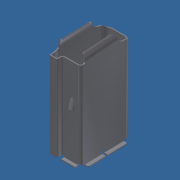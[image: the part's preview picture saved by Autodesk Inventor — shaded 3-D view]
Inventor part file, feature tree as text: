
AUTODESK INVENTOR PART (.ipt)
format: ipt  version: unknown  size: 579,072 bytes
history: native  units: mm
features: sketch x17, extrude x14, other x12, fillet x6, projected_geometry x2, shell x1
ambient origin geometry x8: Origin, YZ Plane, XZ Plane, XY Plane, X Axis, Y Axis, Z Axis, Center Point
feature tree (52):
  extrude  "Выдавливание1"  Depth=38.0mm
  other  "РабПлоскость1"
  other  "РабПлоскость2"
  sketch  "Эскиз4"
  other  "РабПлоскость3"
  extrude  "Выдавливание2"  Depth=42.0mm
  fillet  "Сопряжение7"  Radius=6.0mm
  shell  "Оболочка1"  Thickness=18.5mm
  extrude  "Выдавливание4"  Depth=10.0mm
  extrude  "Выдавливание5"  Depth=13.0mm
  fillet  "Сопряжение8"  Radius=5.0mm
  fillet  "Сопряжение9"  Radius=2.0mm
  extrude  "Выдавливание6"  Depth=64.0mm TaperAngle=0.0deg
  fillet  "Сопряжение10"  Radius=1.0mm
  fillet  "Сопряжение11"  Radius=29.0mm
  fillet  "Сопряжение12"  [1 undecoded]
  extrude  "Выдавливание7"  Depth=4.0mm
  extrude  "Выдавливание8"  Depth=6.0mm
  extrude  "Выдавливание9"  Depth=10.0mm TaperAngle=0.0deg
  other  "РабПлоскость4"
  extrude  "Выдавливание10"  Depth=0.6mm
  extrude  "Выдавливание11"  Depth=0.8mm
  other  "Сгиб детали1"
  extrude  "Выдавливание12"  Depth=29.0mm
  other  "Сгиб детали2"
  extrude  "Выдавливание14"  Depth=3.0mm
  extrude  "Выдавливание15"  Depth=10.0mm
  other  "РабПлоскость5"
  extrude  "Выдавливание16"  Depth=3.5mm
  sketch  "Эскиз1"
  sketch  "Эскиз5"
  sketch  "Эскиз8"
  sketch  "Эскиз9"
  sketch  "Эскиз10"
  sketch  "Эскиз11"
  sketch  "Эскиз12"
  sketch  "Эскиз13"
  sketch  "Эскиз15"
  projected_geometry  "Спроецированная петля1"
  sketch  "Эскиз16"
  sketch  "Эскиз17"
  sketch  "Эскиз18"
  sketch  "Эскиз19"
  sketch  "Эскиз20"
  projected_geometry  "Спроецированная петля2"
  sketch  "Эскиз21"
  sketch  "Эскиз22"
  other  "Проецирование ребер3"
  other  "Проецирование ребер4"
  other  "Проецирование ребер5"
  other  "Проецирование ребер6"
  other  "Проецирование ребер7"
note: 1 required parameter value undecoded (feature->parameter linkage not recoverable at this tier; creation-order binding heuristic only, values carry confidence <= 0.55)
